# Revit family: RobeHook_SurfaceMount_Nero_Mecca_Slim
name_source: partatom
category: Specialty Equipment
units: mm (PartAtom-declared; Revit-internal decimal feet)

## family parameters
Always vertical = Yes
Cut with Voids When Loaded = Yes
Maintain Annotation Orientation = No
OmniClass Number = 23.31.25.27
OmniClass Title = Robe Hooks
Part Type = Normal
Room Calculation Point = No
Round Connector Dimension = Use Diameter
Shared = No
Work Plane-Based = No

## types (7) — shared parameters
Assembly Code = C1030220
Default Elevation = 1050 mm
IfcExportAs = IfcFurnitureType
IfcExportType = USERDEFINED
Manufacturer = Nero
ManufacturerOverallDepth = 55 mm  [stored 0.180446 ft]
ManufacturerOverallHeight = 35 mm  [stored 0.114829 ft]
ManufacturerOverallWidth = 35 mm  [stored 0.114829 ft]
ManufacturerURLProductSpecific = https://nerotapware.com.au
ModifiedIssue = 20251105 $
URL = https://nerotapware.com.au
Uniclass2015Code = Pr_40_30_78_15
Uniclass2015Title = Clothes Hooks
Uniclass2015Version = Products v1.35

## per-type parameters (varying)
| type | Description | ManufacturerSpecCode | Material | Model | Type Comments |
| Matte White (NR1982BMW) | Mecca Robe Hook Slim Matte White | NR1982BMW | Metal_MatteWhite_Nero | NR1982BMW | Robe Hook - Surface Mount - Slim - Matte White |
| Matte Black (NR1982BMB) | Mecca Robe Hook Slim Matte Black | NR1982BMB | Metal_MatteBlack_Nero | NR1982BMB | Robe Hook - Surface Mount - Slim - Matte Black |
| Brushed Gold (NR1982BBG) | Mecca Robe Hook Slim Brushed Gold | NR1982BBG | Metal_Gold_Nero_Brushed | NR1982BBG | Robe Hook - Surface Mount - Slim - Brushed Gold |
| Brushed Bronze (NR1982BBZ) | Mecca Robe Hook Slim Brushed Bronze | NR1982BBZ | Metal_Bronze_Nero_Brushed | NR1982BBZ | Robe Hook - Surface Mount - Slim - Brushed Bronze |
| Brushed Nickel (NR1982BBN) | Mecca Robe Hook Slim Brushed Nickel | NR1982BBN | Metal_Nickel_Nero_Brushed | NR1982BBN | Robe Hook - Surface Mount - Slim - Brushed Nickel |
| Gunmetal (NR1982BGM) | Mecca Robe Hook Slim Gun Metal | NR1982BGM | Metal_GunMetal_Nero | NR1982BGM | Robe Hook - Surface Mount - Slim - Gunmetal |
| Chrome (NR1982BCH) | Mecca Robe Hook Slim Chrome | NR1982BCH | Metal_Chrome_Nero | NR1982BCH | Robe Hook - Surface Mount - Slim - Chrome |

note: [stored X ft] marks values corroborated as IEEE doubles in the binary element streams (Revit-internal decimal feet)

## geometry (parser evidence)
native form markers: Sweep x3
no freeform markers — native parametric forms only
